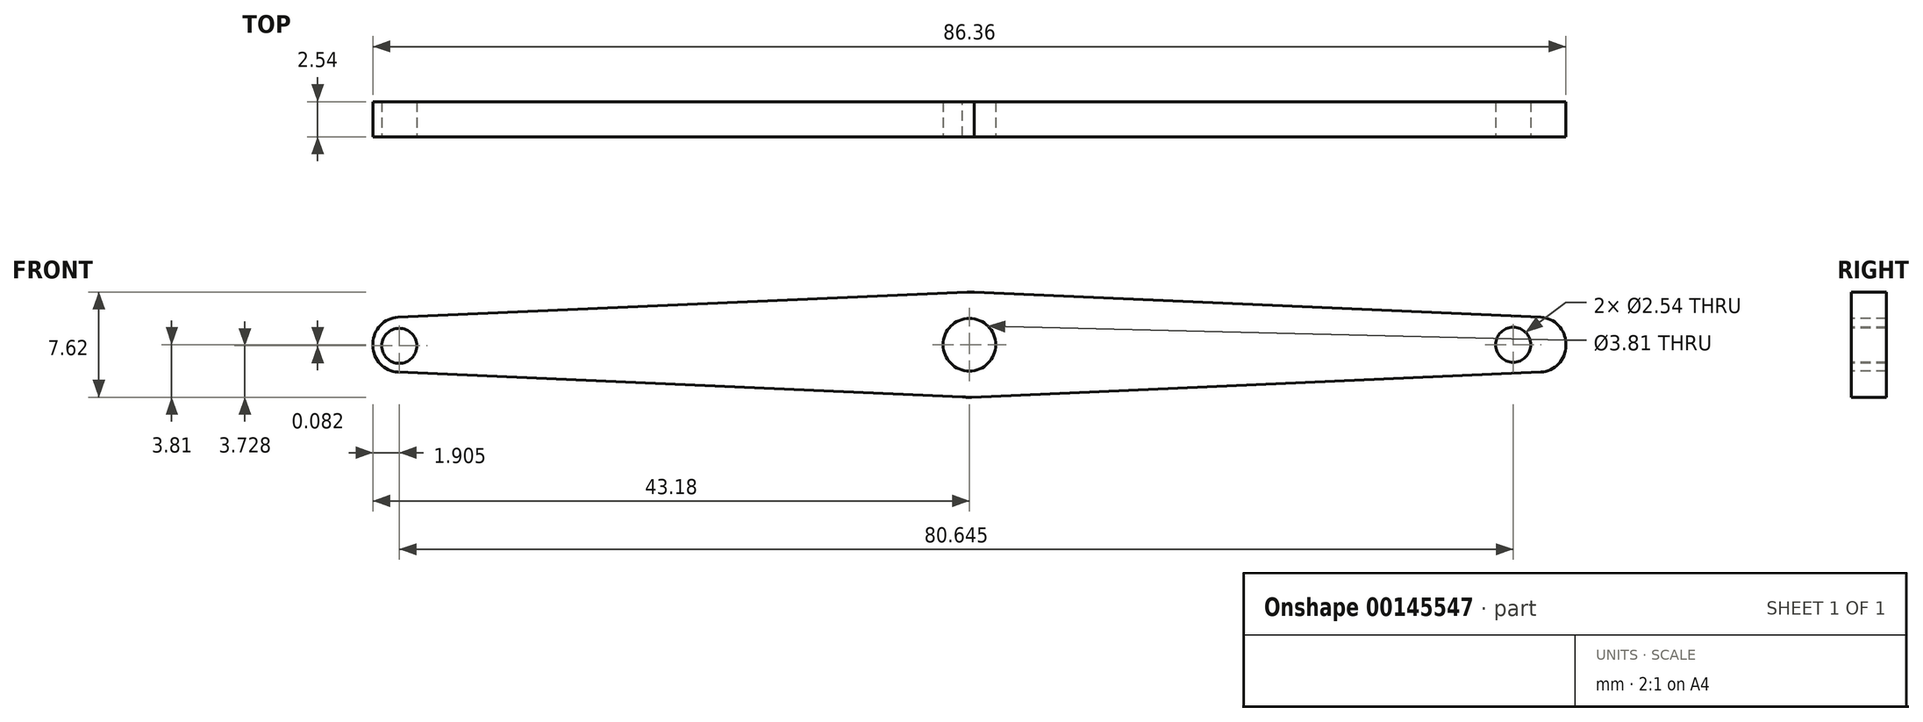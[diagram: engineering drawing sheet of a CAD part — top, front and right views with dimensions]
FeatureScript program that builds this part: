
annotation { "Feature Type Name" : "Feature", "Feature Type Description" : "" }
export const myFeature = defineFeature(function(context is Context, id is Id, definition is map)
    precondition{}
    {
        {
            var Q0;
            Q0=qCreatedBy(makeId("Front.planeOp"),FACE);
            var sketch = newSketch(context, id + "F0", { "sketchPlane" : qUnion([Q0])});
            skCircle(sketch, "E0", {"center": v(0, 0) * mm, "radius": 3.8 * mm});
            skLineSegment(sketch, "E1", {"start": v(0, 3.81) * mm, "end": v(43.18, 1.9) * mm});
            skLineSegment(sketch, "E2", {"start": v(43.18, 1.9) * mm, "end": v(43.18, -1.9) * mm});
            skLineSegment(sketch, "E3", {"start": v(43.18, -1.9) * mm, "end": v(0, -3.81) * mm});
            skLineSegment(sketch, "E4", {"start": v(-0.17, 3.8) * mm, "end": v(-43.18, 1.9) * mm});
            skLineSegment(sketch, "E5", {"start": v(-43.18, 1.9) * mm, "end": v(-43.18, -1.9) * mm});
            skLineSegment(sketch, "E6", {"start": v(-43.18, -1.9) * mm, "end": v(0.17, -3.8) * mm});
            skSolve(sketch);
        }
        {
            var Q0;
            Q0 = qSketchRegion(id + "F0", true);
            extrude(context, id + "F1", {"entities" : qUnion([Q0]), "depth" : 2.54 * mm});
        }
        {
            var Q0;
            Q0=makeQuery(id+"F1.opExtrude","SWEPT_EDGE",EDGE,{"disambiguationData":[OSD([sQuery(id+"F0.wireOp",EDGE,"E2"),sQuery(id+"F0.wireOp",EDGE,"E3")])]});
            var Q1;
            Q1=makeQuery(id+"F1.opExtrude","SWEPT_EDGE",EDGE,{"disambiguationData":[OSD([sQuery(id+"F0.wireOp",EDGE,"E1"),sQuery(id+"F0.wireOp",EDGE,"E2")])]});
            var Q2;
            Q2=makeQuery(id+"F1.opExtrude","SWEPT_EDGE",EDGE,{"disambiguationData":[OSD([sQuery(id+"F0.wireOp",EDGE,"E4"),sQuery(id+"F0.wireOp",EDGE,"E5")])]});
            var Q3;
            Q3=makeQuery(id+"F1.opExtrude","SWEPT_EDGE",EDGE,{"disambiguationData":[OSD([sQuery(id+"F0.wireOp",EDGE,"E5"),sQuery(id+"F0.wireOp",EDGE,"E6")])]});
            fillet(context, id + "F2", {"entities" : qUnion([Q0, Q1, Q2, Q3]), "radius" : 1.9 * mm, "tangentPropagation" : true, "allowEdgeOverflow" : false});
        }
        {
            var Q0;
            Q0=makeQuery(id+"F1.opExtrude","CAP_FACE",FACE,{"disambiguationData":[OSD([sQuery(id+"F0.wireOp",EDGE,"E0"),sQuery(id+"F0.wireOp",EDGE,"E1"),sQuery(id+"F0.wireOp",EDGE,"E2"),sQuery(id+"F0.wireOp",EDGE,"E3"),sQuery(id+"F0.wireOp",EDGE,"E4"),sQuery(id+"F0.wireOp",EDGE,"E5"),sQuery(id+"F0.wireOp",EDGE,"E6")])],"isStart":false});
            var sketch = newSketch(context, id + "F3", { "sketchPlane" : qUnion([Q0])});
            skCircle(sketch, "E7", {"center": v(0, 0) * mm, "radius": 1.9 * mm});
            skCircle(sketch, "E8", {"center": v(39.37, 0) * mm, "radius": 1.27 * mm});
            skCircle(sketch, "E9", {"center": v(-41.28, -0.08) * mm, "radius": 1.27 * mm});
            skSolve(sketch);
        }
        {
            var Q0;
            Q0 = qSketchRegion(id + "F3", true);
            extrude(context, id + "F4", {"entities" : qUnion([Q0]), "operationType" : NewBodyOperationType.REMOVE, "endBound" : BoundingType.THROUGH_ALL, "oppositeDirection" : true, "depth" : 25.4 * mm});
        }
    });
